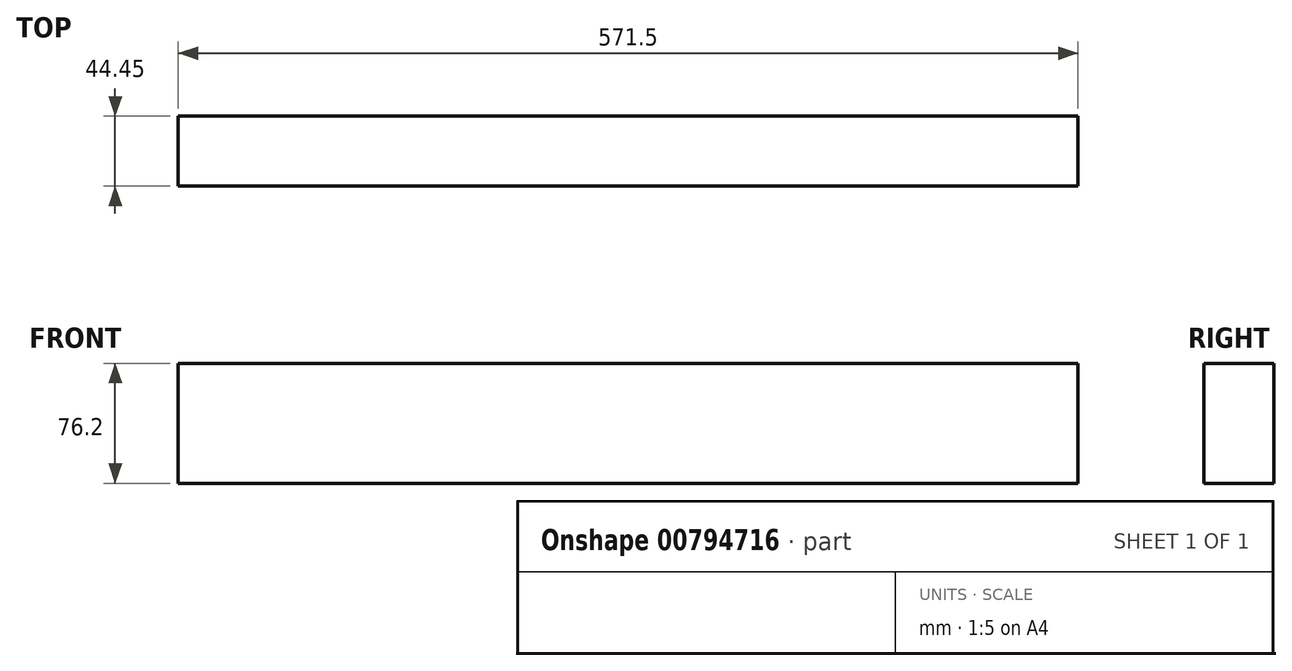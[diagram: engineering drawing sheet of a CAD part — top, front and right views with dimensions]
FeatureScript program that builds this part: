
annotation { "Feature Type Name" : "Feature", "Feature Type Description" : "" }
export const myFeature = defineFeature(function(context is Context, id is Id, definition is map)
    precondition{}
    {
        {
            var Q0;
            Q0=qCreatedBy(makeId("Front.planeOp"),FACE);
            var sketch = newSketch(context, id + "F0", { "sketchPlane" : qUnion([Q0])});
            skLineSegment(sketch, "E0.bottom", {"start": v(285.75, -38.1) * mm, "end": v(-285.75, -38.1) * mm});
            skLineSegment(sketch, "E0.top", {"start": v(285.75, 38.1) * mm, "end": v(-285.75, 38.1) * mm});
            skLineSegment(sketch, "E0.left", {"start": v(285.75, -38.1) * mm, "end": v(285.75, 38.1) * mm});
            skLineSegment(sketch, "E0.right", {"start": v(-285.75, -38.1) * mm, "end": v(-285.75, 38.1) * mm});
            skPoint(sketch, "E0.middle", {"position": v(0, 0) * mm});
            skSolve(sketch);
        }
        {
            var Q0;
            Q0=makeQuery(id+"F0.imprint","IMPRINT",FACE,{"disambiguationData":[TD([[makeQuery(id+"F0.imprint","IMPRINT",EDGE,{"derivedFrom":sQuery(id+"F0.wireOp",EDGE,"E0.bottom")}),-1.0]])]});
            extrude(context, id + "F1", {"entities" : qUnion([Q0]), "depth" : 44.45 * mm, "offsetDistance" : 25.4 * mm});
        }
    });
